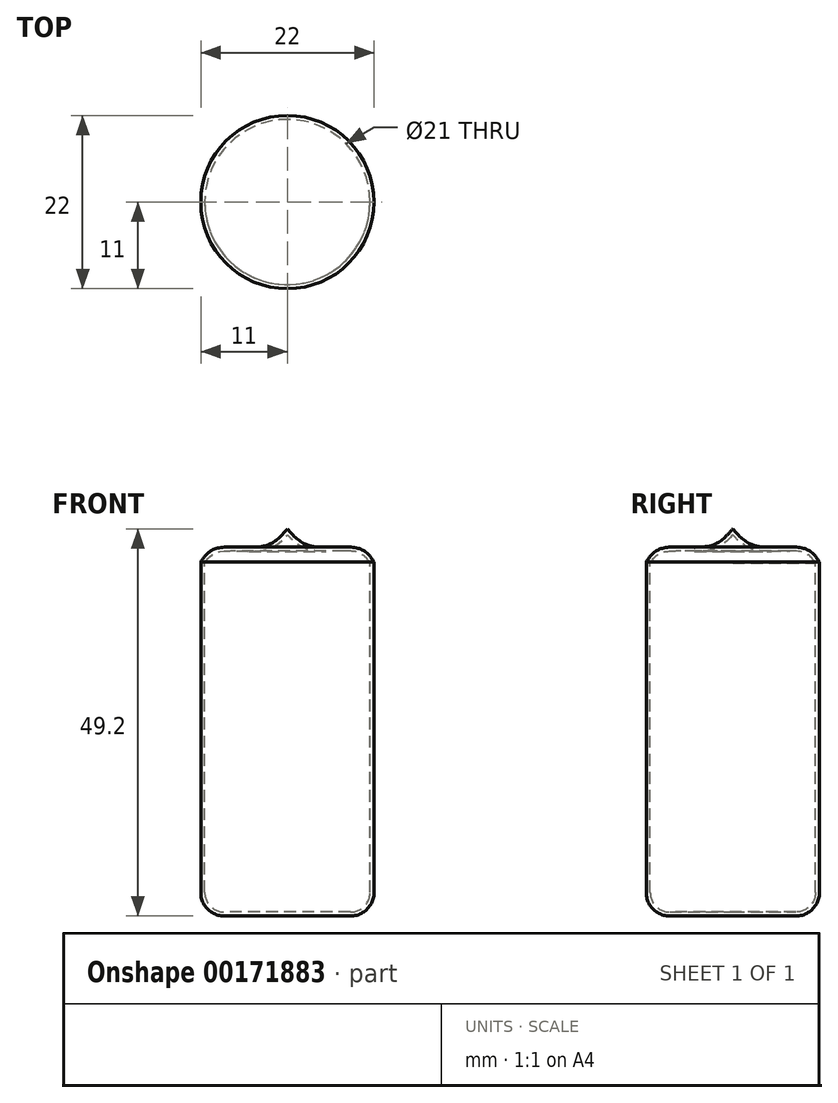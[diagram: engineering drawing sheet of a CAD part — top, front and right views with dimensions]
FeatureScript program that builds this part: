
annotation { "Feature Type Name" : "Feature", "Feature Type Description" : "" }
export const myFeature = defineFeature(function(context is Context, id is Id, definition is map)
    precondition{}
    {
        {
            var Q0;
            Q0=qCreatedBy(makeId("Front.planeOp"),FACE);
            var sketch = newSketch(context, id + "F0", { "sketchPlane" : qUnion([Q0])});
            skLineSegment(sketch, "E0", {"start": v(-8, 0) * mm, "end": v(0, 0) * mm});
            skLineSegment(sketch, "E1", {"start": v(0, 33.7) * mm, "end": v(0, 0) * mm, "construction": true});
            skLineSegment(sketch, "E2", {"start": v(-11, 3) * mm, "end": v(-11, 45) * mm});
            skPoint(sketch, "E3.visualSharp", {"position": v(-16, 0) * mm});
            skArc(sketch, "E3.filletArc", {"start": v(-11, 3) * mm, "mid": v(-10.12, 0.88) * mm, "end": v(-8, 0) * mm});
            skLineSegment(sketch, "E4", {"start": v(-16, 0) * mm, "end": v(-8, 0) * mm});
            skPoint(sketch, "E5.end.orphan", {"position": v(0, 107.62) * mm});
            skPoint(sketch, "E6.visualSharp", {"position": v(-11, 45.64) * mm});
            skLineSegment(sketch, "E7", {"start": v(0, 43.04) * mm, "end": v(0, 55.36) * mm, "construction": true});
            skLineSegment(sketch, "E8", {"start": v(0, 49.2) * mm, "end": v(0, 0) * mm});
            skLineSegment(sketch, "E9.trimOffspring", {"start": v(0, 0) * mm, "end": v(0, -19.5) * mm, "construction": true});
            skFitSpline(sketch, "E10", {"points": [v(-11, 45) * mm, v(-9.01, 46.7) * mm, v(-2.95, 47.01) * mm, v(0, 49.2) * mm], "startDerivative": vector(5.42, 7.91) * mm, "endDerivative": vector(7.38, 8.72) * mm});
            skSolve(sketch);
        }
        {
            var Q0;
            {var subQ1=sQuery(id+"F0.wireOp",EDGE,"E0");Q0=makeQuery(id+"F0.imprint","IMPRINT",FACE,{"disambiguationData":[TD([[makeQuery(id+"F0.imprint","IMPRINT",EDGE,{"derivedFrom":subQ1}),1.0]])]});}
            var Q1;
            Q1=sQuery(id+"F0.wireOp",EDGE,"E8");
            revolve(context, id + "F1", {"entities" : qUnion([Q0]), "axis" : qUnion([Q1]), "revolveType" : RevolveType.FULL});
        }
        {
            var Q0;
            Q0=makeQuery(id+"F1.opRevolve","SWEPT_FACE",FACE,{"disambiguationData":[OSD([sQuery(id+"F0.wireOp",EDGE,"E2")])]});
            var Q1;
            Q1=makeQuery(id+"F1.opRevolve","SWEPT_FACE",FACE,{"disambiguationData":[OSD([sQuery(id+"F0.wireOp",EDGE,"hlonBQOj-Ca6K-z7PR-3W5p-bjjZtAkgobDa")])]});
            var Q2;
            Q2=makeQuery(id+"F1.opRevolve","SWEPT_BODY",BODY,{"disambiguationData":[OSD([sQuery(id+"F0.wireOp",EDGE,"E0"),sQuery(id+"F0.wireOp",EDGE,"E2"),sQuery(id+"F0.wireOp",EDGE,"E3.filletArc"),sQuery(id+"F0.wireOp",EDGE,"hlonBQOj-Ca6K-z7PR-3W5p-bjjZtAkgobDa"),sQuery(id+"F0.wireOp",EDGE,"E6.filletArc"),sQuery(id+"F0.wireOp",EDGE,"E8")])]});
            shell(context, id + "F2", {"isHollow" : true, "entities" : qUnion([Q0, Q1]), "parts" : qUnion([Q2]), "thickness" : 0.5 * mm});
        }
    });
